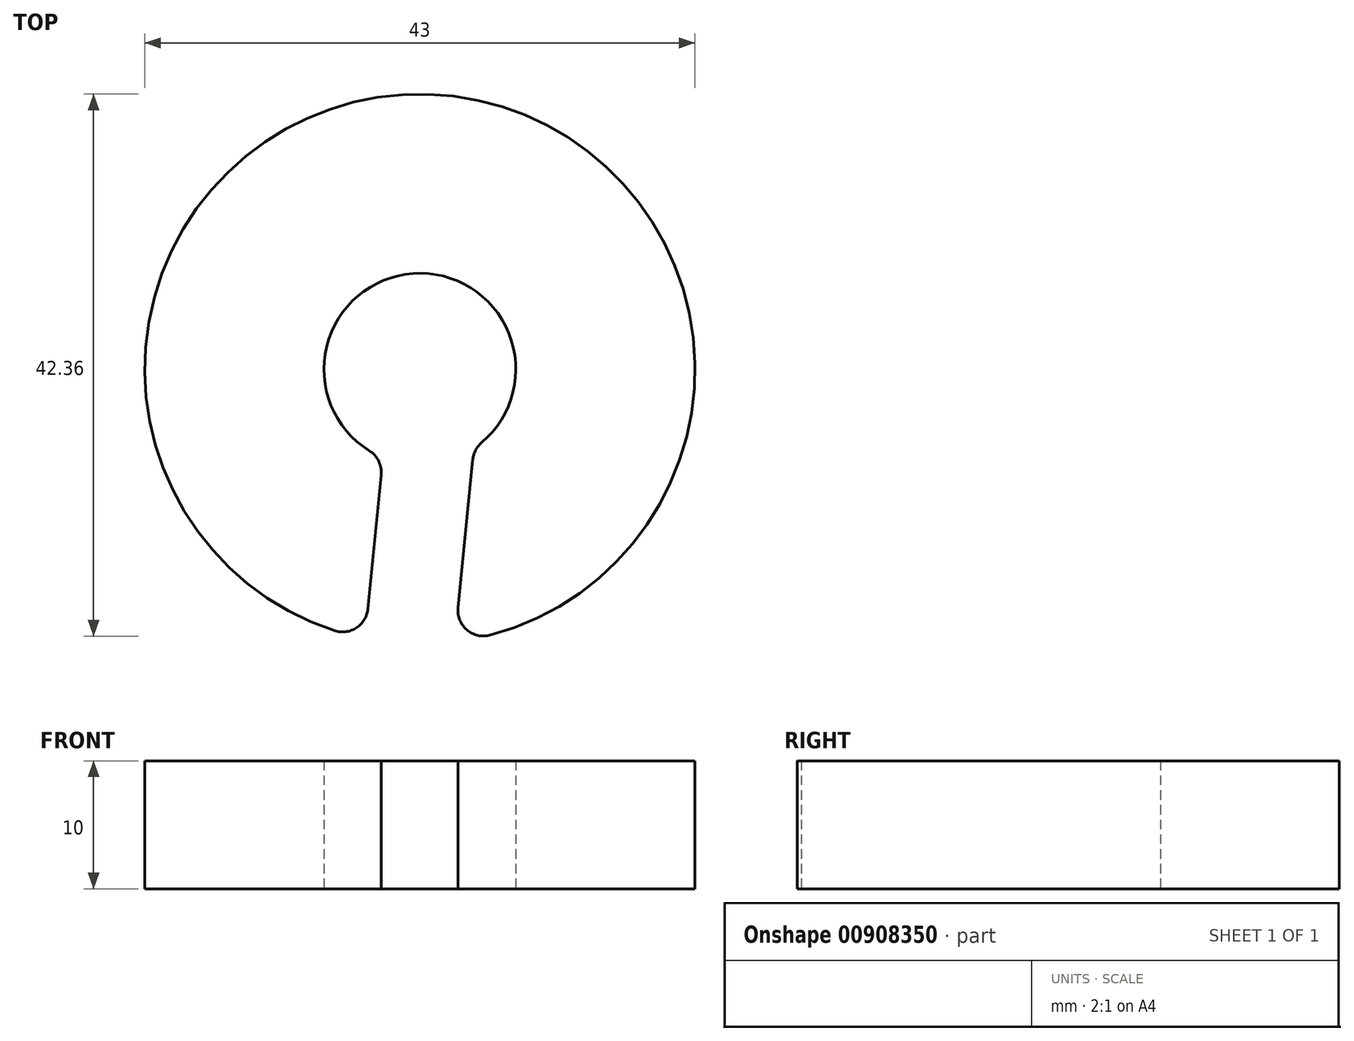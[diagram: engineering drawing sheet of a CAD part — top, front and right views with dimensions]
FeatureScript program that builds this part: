
annotation { "Feature Type Name" : "Feature", "Feature Type Description" : "" }
export const myFeature = defineFeature(function(context is Context, id is Id, definition is map)
    precondition{}
    {
        {
            var Q0;
            Q0=qCreatedBy(makeId("Top.planeOp"),FACE);
            var sketch = newSketch(context, id + "F0", { "sketchPlane" : qUnion([Q0])});
            skArc(sketch, "E0", {"start": v(4.21, -6.2) * mm, "mid": v(-0.75, 7.46) * mm, "end": v(-2.9, -6.92) * mm});
            skArc(sketch, "E1", {"start": v(0, -21.5) * mm, "mid": v(2.16, 21.4) * mm, "end": v(-4.3, -21.07) * mm});
            skLineSegment(sketch, "E2", {"start": v(0, 0) * mm, "end": v(0, -21.5) * mm});
            skLineSegment(sketch, "E3", {"start": v(0, -21.5) * mm, "end": v(0, -7.5) * mm});
            skLineSegment(sketch, "E4.bottom", {"start": v(2.27, -25.8) * mm, "end": v(-4.7, -25.23) * mm});
            skLineSegment(sketch, "E4.left", {"start": v(2.27, -25.8) * mm, "end": v(4.7, -1.25) * mm});
            skLineSegment(sketch, "E4.right", {"start": v(-4.3, -21.07) * mm, "end": v(-2.27, -0.67) * mm});
            skPoint(sketch, "E4.middle", {"position": v(0, -13.24) * mm});
            skSolve(sketch);
        }
        {
            var Q0;
            {var subQ0=sQuery(id+"F0.wireOp",EDGE,"E3");var subQ1=sQuery(id+"F0.wireOp",EDGE,"E0");var subQ2=makeQuery(id+"F0.imprint","INTERSECT",VERTEX,{"derivedFrom":[subQ1,subQ0]});Q0=makeQuery(id+"F0.imprint","IMPRINT",FACE,{"disambiguationData":[TD([[makeQuery(id+"F0.imprint","IMPRINT",EDGE,{"disambiguationData":[TD([[subQ2,-1.0]])],"derivedFrom":subQ1}),-1.0]])]});}
            var sketch = newSketch(context, id + "F1", { "sketchPlane" : qUnion([Q0])});
            skSolve(sketch);
        }
        {
            var Q0;
            {var subQ0=sQuery(id+"F0.wireOp",EDGE,"E3");var subQ1=sQuery(id+"F0.wireOp",EDGE,"E0");var subQ2=makeQuery(id+"F0.imprint","INTERSECT",VERTEX,{"derivedFrom":[subQ1,subQ0]});Q0=makeQuery(id+"F1.imprint","IMPRINT",FACE,{"disambiguationData":[TD([[makeQuery(id+"F1.imprint","IMPRINT",EDGE,{"derivedFrom":makeQuery(id+"F0.imprint","IMPRINT",EDGE,{"disambiguationData":[TD([[subQ2,-1.0]])],"derivedFrom":subQ1})}),-1.0]])]});}
            extrude(context, id + "F2", {"entities" : qUnion([Q0]), "depth" : 10 * mm, "offsetDistance" : 25 * mm});
        }
        {
            var Q0;
            Q0=makeQuery(id+"F2.opExtrude","SWEPT_EDGE",EDGE,{"disambiguationData":[OSD([sQuery(id+"F0.wireOp",EDGE,"E1"),sQuery(id+"F0.wireOp",EDGE,"E4.left")])]});
            var Q1;
            Q1=makeQuery(id+"F2.opExtrude","SWEPT_EDGE",EDGE,{"disambiguationData":[OSD([sQuery(id+"F0.wireOp",EDGE,"E1"),sQuery(id+"F0.wireOp",EDGE,"E4.right")])]});
            var Q2;
            Q2=makeQuery(id+"F2.opExtrude","SWEPT_EDGE",EDGE,{"disambiguationData":[OSD([sQuery(id+"F0.wireOp",EDGE,"E0"),sQuery(id+"F0.wireOp",EDGE,"E4.right")])]});
            var Q3;
            Q3=makeQuery(id+"F2.opExtrude","SWEPT_EDGE",EDGE,{"disambiguationData":[OSD([sQuery(id+"F0.wireOp",EDGE,"E0"),sQuery(id+"F0.wireOp",EDGE,"E4.left")])]});
            fillet(context, id + "F3", {"entities" : qUnion([Q0, Q1, Q2, Q3]), "radius" : 2 * mm, "tangentPropagation" : true, "allowEdgeOverflow" : false});
        }
    });
